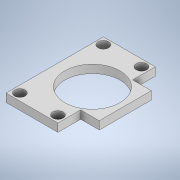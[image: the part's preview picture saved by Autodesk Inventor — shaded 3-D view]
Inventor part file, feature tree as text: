
AUTODESK INVENTOR PART (.ipt)
format: ipt  version: 2020.1 (Build 241239000, 239)  size: 132,608 bytes
history: native  units: mm
features: other x1, extrude x1, sketch x1
ambient origin geometry x8: Origin, YZ Plane, XZ Plane, XY Plane, X Axis, Y Axis, Z Axis, Center Point
bodies: Body1 (feature_tree)
feature tree (3):
  other  "Твердое тело1"
  extrude  "Выдавливание1"  Depth=5.0mm TaperAngle=0.0deg
  sketch  "Эскиз1"
